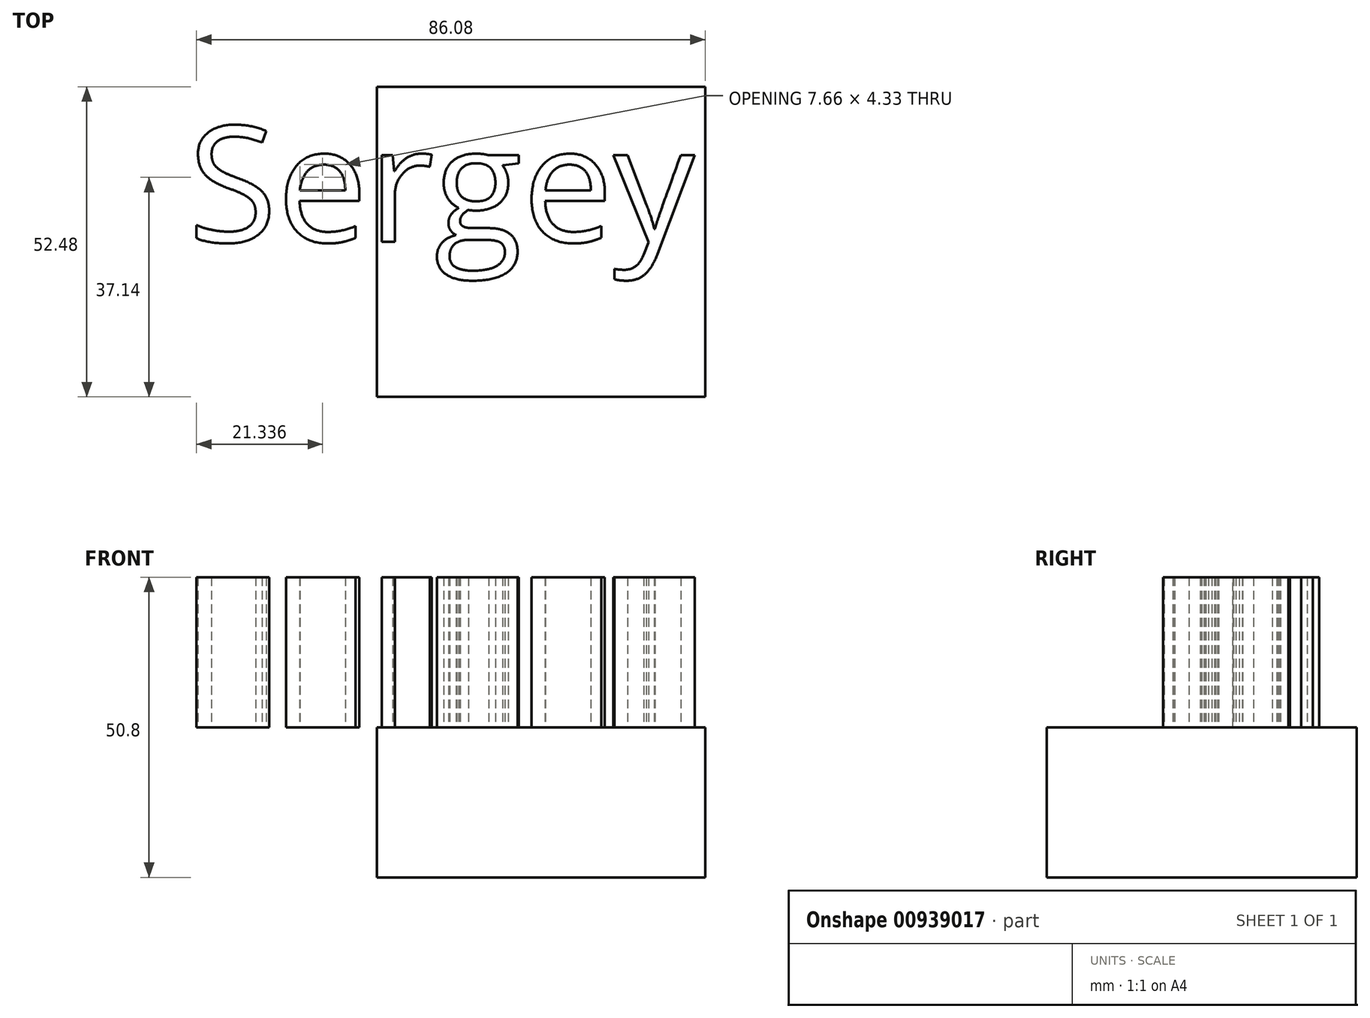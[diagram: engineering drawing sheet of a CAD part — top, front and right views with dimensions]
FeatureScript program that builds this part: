
annotation { "Feature Type Name" : "Feature", "Feature Type Description" : "" }
export const myFeature = defineFeature(function(context is Context, id is Id, definition is map)
    precondition{}
    {
        {
            var Q0;
            Q0=qCreatedBy(makeId("Top.planeOp"),FACE);
            var sketch = newSketch(context, id + "F0", { "sketchPlane" : qUnion([Q0])});
            skLineSegment(sketch, "E0.bottom", {"start": v(-24.75, 22.07) * mm, "end": v(30.8, 22.07) * mm});
            skLineSegment(sketch, "E0.top", {"start": v(-24.75, -30.4) * mm, "end": v(30.8, -30.4) * mm});
            skLineSegment(sketch, "E0.left", {"start": v(-24.75, 22.07) * mm, "end": v(-24.75, -30.4) * mm});
            skLineSegment(sketch, "E0.right", {"start": v(30.8, 22.07) * mm, "end": v(30.8, -30.4) * mm});
            skSolve(sketch);
        }
        {
            var Q0;
            Q0=makeQuery(id+"F0.imprint","IMPRINT",FACE,{"disambiguationData":[TD([[makeQuery(id+"F0.imprint","IMPRINT",EDGE,{"derivedFrom":sQuery(id+"F0.wireOp",EDGE,"E0.bottom")}),-1.0]])]});
            extrude(context, id + "F1", {"entities" : qUnion([Q0]), "depth" : 25.4 * mm, "offsetDistance" : 25.4 * mm});
        }
        {
            var Q0;
            Q0=makeQuery(id+"F1.opExtrude","CAP_FACE",FACE,{"disambiguationData":[OSD([sQuery(id+"F0.wireOp",EDGE,"E0.bottom"),sQuery(id+"F0.wireOp",EDGE,"E0.top"),sQuery(id+"F0.wireOp",EDGE,"E0.left"),sQuery(id+"F0.wireOp",EDGE,"E0.right")])],"isStart":false});
            var sketch = newSketch(context, id + "F2", { "sketchPlane" : qUnion([Q0])});
            skText(sketch, "E1", { "text": "Sergey", "fontName": "OpenSans-Regular.ttf"});
            const initialGuessF2  = {"E1": [-0.0567, -0.00417, 1, 0, 0.01972]};
            skSetInitialGuess(sketch, initialGuessF2);
            skSolve(sketch);
        }
        {
            var Q0;
            Q0 = qSketchRegion(id + "F2", true);
            var sketch = newSketch(context, id + "F3", { "sketchPlane" : qUnion([Q0])});
            skSolve(sketch);
        }
        {
            var Q0;
            Q0 = qSketchRegion(id + "F2", true);
            extrude(context, id + "F4", {"entities" : qUnion([Q0]), "operationType" : NewBodyOperationType.ADD, "depth" : 25.4 * mm, "offsetDistance" : 25.4 * mm});
        }
        {
            var Q0;
            {var subQ0=sQuery(id+"F0.wireOp",EDGE,"E0.right");var subQ1=sQuery(id+"F0.wireOp",EDGE,"E0.left");var subQ2=sQuery(id+"F0.wireOp",EDGE,"E0.top");var subQ3=sQuery(id+"F0.wireOp",EDGE,"E0.bottom");Q0=makeQuery(id+"F4.boolean.opBoolean","SPLIT",FACE,{"disambiguationData":[TD([makeQuery(id+"F1.opExtrude","SWEPT_FACE",FACE,{"disambiguationData":[OSD([subQ3])]})])],"derivedFrom":makeQuery(id+"F1.opExtrude","CAP_FACE",FACE,{"disambiguationData":[OSD([subQ3,subQ2,subQ1,subQ0])],"isStart":false})});}
            var sketch = newSketch(context, id + "F5", { "sketchPlane" : qUnion([Q0])});
            skSolve(sketch);
        }
        {
            var Q0;
            Q0=makeQuery(id+"F3.imprint","IMPRINT",FACE,{"disambiguationData":[TD([[makeQuery(id+"F3.imprint","IMPRINT",EDGE,{"derivedFrom":makeQuery(id+"F2.imprint","IMPRINT",EDGE,{"derivedFrom":sQuery(id+"F2.wireOp",EDGE,"E1.sketch_text.stroke-0")})}),-1.0]])]});
            extrude(context, id + "F6", {"entities" : qUnion([Q0]), "operationType" : NewBodyOperationType.ADD, "depth" : 25.4 * mm, "offsetDistance" : 25.4 * mm});
        }
    });
